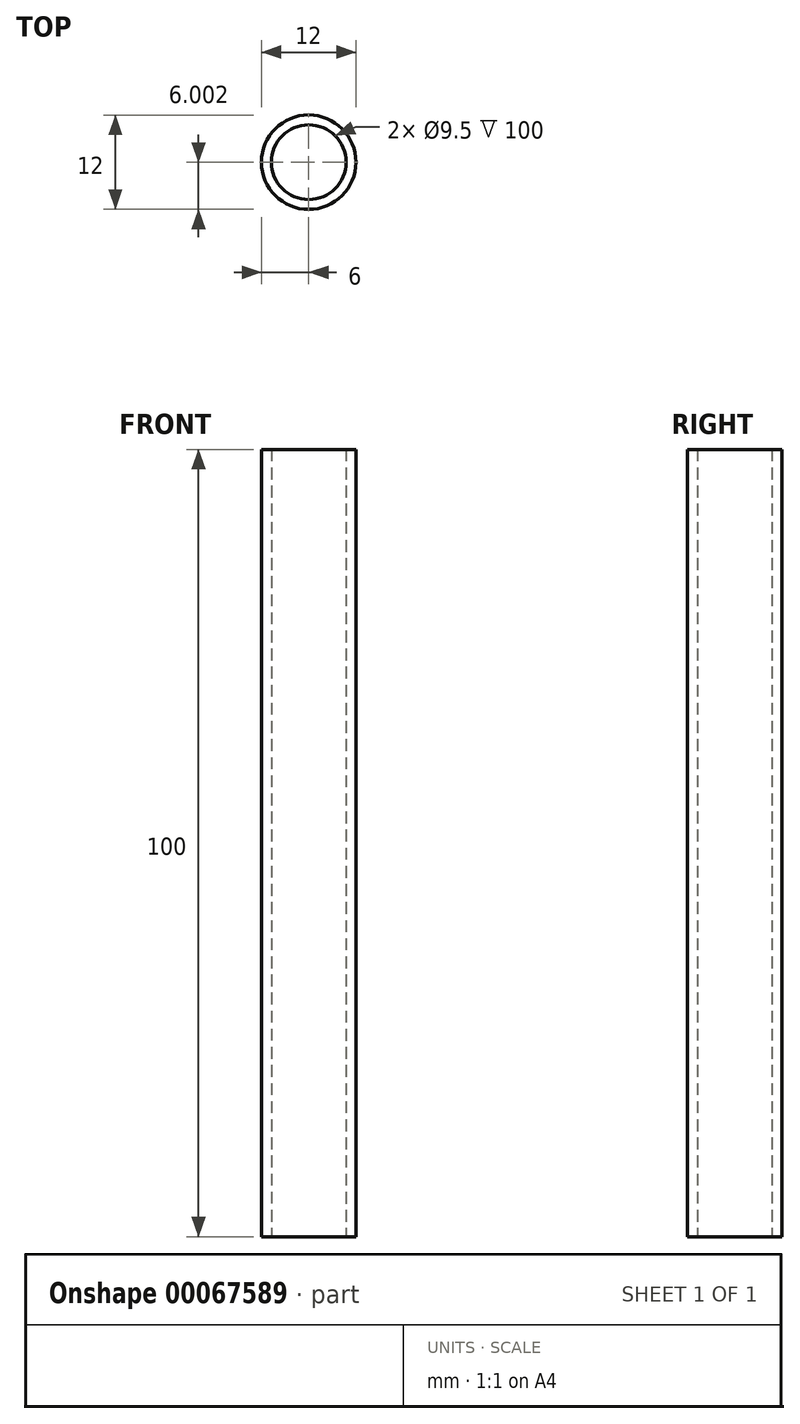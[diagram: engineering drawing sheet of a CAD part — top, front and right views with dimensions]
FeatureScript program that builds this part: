
annotation { "Feature Type Name" : "Feature", "Feature Type Description" : "" }
export const myFeature = defineFeature(function(context is Context, id is Id, definition is map)
    precondition{}
    {
        {
            var Q0;
            Q0=qCreatedBy(makeId("Top.planeOp"),FACE);
            var sketch = newSketch(context, id + "F0", { "sketchPlane" : qUnion([Q0])});
            skCircle(sketch, "E0", {"center": v(0, -7.98) * mm, "radius": 6 * mm});
            skCircle(sketch, "E1", {"center": v(0, -7.98) * mm, "radius": 4.75 * mm});
            skSolve(sketch);
        }
        {
            var Q0;
            Q0 = qSketchRegion(id + "F0", true);
            extrude(context, id + "F1", {"entities" : qUnion([Q0]), "depth" : 100 * mm});
        }
    });
